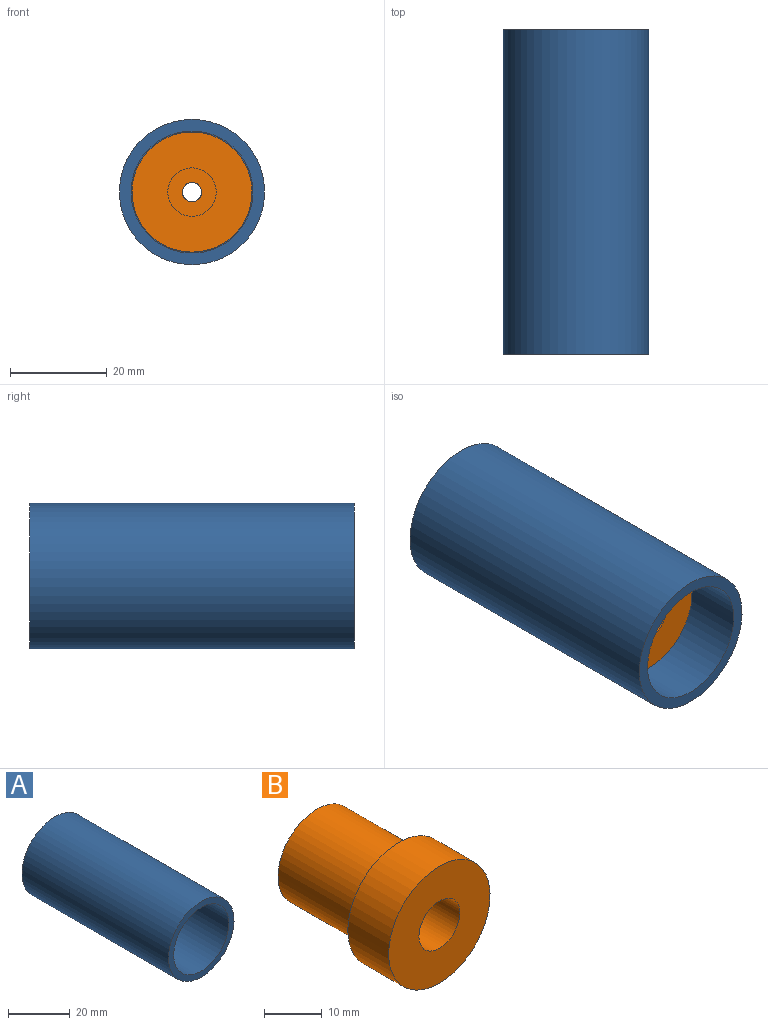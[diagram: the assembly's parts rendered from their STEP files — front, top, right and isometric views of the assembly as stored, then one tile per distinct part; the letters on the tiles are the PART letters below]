
ASSEMBLY  parts=2 mates=1
PART A: 8 faces, bbox 30x67x30 mm
  f0: plane 30x30mm, normal (0,1,0), area 643.2mm2, adj f1,f7
  f1: cylinder r=4.5mm len=20mm, axis (0,1,0), area 565.5mm2, adj f0,f2
  f2: plane 9x9mm, normal (0,1,0), area 51.1mm2, adj f1,f3
  f3: cylinder r=2mm len=5mm, axis (0,1,0), area 62.8mm2, adj f2,f4
  f4: plane 25.2x25.2mm, normal (0,-1,0), area 486.2mm2, adj f3,f5
  f5: cylinder r=12.6mm len=42mm, axis (0,1,0), area 3325.1mm2, adj f4,f6
  f6: plane 30x30mm, normal (0,-1,0), area 208.1mm2, adj f5,f7
  f7: cylinder r=15mm len=67mm, axis (0,1,0), area 6314.6mm2, adj f0,f6
PART B: 8 faces, bbox 24.8x30x24.8 mm
  f0: plane 19x19mm, normal (0,1,0), area 271mm2, adj f1,f7
  f1: cylinder r=2mm len=20mm, axis (0,-1,0), area 251.3mm2, adj f0,f2
  f2: plane 10x10mm, normal (0,-1,0), area 66mm2, adj f1,f3
  f3: cylinder r=5mm len=10mm, axis (0,-1,0), area 314.2mm2, adj f2,f4
  f4: plane 24.8x24.8mm, normal (0,-1,0), area 404.5mm2, adj f3,f5
  f5: cylinder r=12.4mm len=24.8mm, axis (0,-1,0), area 779.1mm2, adj f4,f6
  f6: plane 24.8x24.8mm, normal (0,1,0), area 199.5mm2, adj f5,f7
  f7: cylinder r=9.5mm len=20mm, axis (0,-1,0), area 1193.8mm2, adj f0,f6
PLACE A t=(0,-12,0)mm
PLACE B at identity fixed
MATE slider B.f1 <-> A.f1  axis (0,1,0) through (0,30,0)mm
